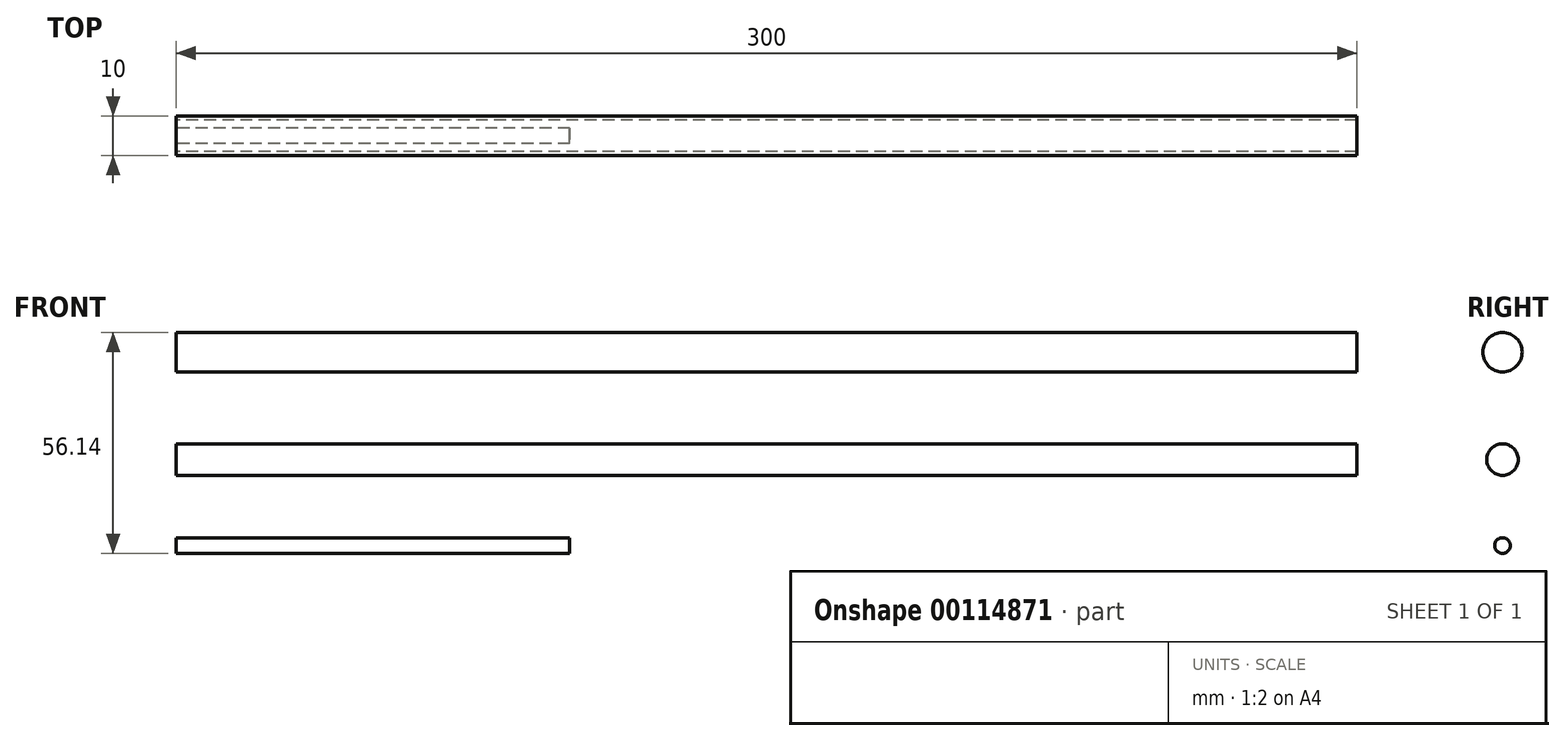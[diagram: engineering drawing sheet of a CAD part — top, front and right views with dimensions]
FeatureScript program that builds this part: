
annotation { "Feature Type Name" : "Feature", "Feature Type Description" : "" }
export const myFeature = defineFeature(function(context is Context, id is Id, definition is map)
    precondition{}
    {
        {
            var Q0;
            Q0=qCreatedBy(makeId("Right.planeOp"),FACE);
            var sketch = newSketch(context, id + "F0", { "sketchPlane" : qUnion([Q0])});
            skCircle(sketch, "E0", {"center": v(0, 0) * mm, "radius": 4 * mm});
            skCircle(sketch, "E1", {"center": v(0, 27.28) * mm, "radius": 5 * mm});
            skSolve(sketch);
        }
        {
            var Q0;
            Q0 = qSketchRegion(id + "F0", true);
            extrude(context, id + "F1", {"entities" : qUnion([Q0]), "depth" : 300 * mm});
        }
        {
            var Q0;
            Q0=qCreatedBy(makeId("Right.planeOp"),FACE);
            var sketch = newSketch(context, id + "F2", { "sketchPlane" : qUnion([Q0])});
            skCircle(sketch, "E2", {"center": v(0, -21.86) * mm, "radius": 2 * mm});
            skSolve(sketch);
        }
        {
            var Q0;
            Q0 = qSketchRegion(id + "F2", true);
            extrude(context, id + "F3", {"entities" : qUnion([Q0]), "depth" : 100 * mm});
        }
    });
